# Revit family: PEFY-WP25VMS1-E_Service_Area1
name_source: partatom
category: Mechanical Equipment
revit_build: Autodesk Revit Architecture 2012 (Build: 20110916_2132(x64)
units: mm (PartAtom-declared; Revit-internal decimal feet)

## types (6) — shared parameters
Airflow Rate_High (m3/h) = 540
Airflow Rate_High (m3/min) = 9
Airflow Rate_Low (m3/h) = 330
Airflow Rate_Low (m3/min) = 5.5
Airflow Rate_Mid (m3/h) = 420
Airflow Rate_Mid (m3/min) = 7
Cooling Capacity (kW) = 2.8
Cooling Current (A) = 0.51
Cooling Power Input (kW) = 0.06
Depth = 700 mm  [stored 2.29659 ft]
Description = Ceiling concealed
Drain pipe1_radius = 16 mm  [stored 0.0524934 ft]
Drain pipe2_radius = 16 mm  [stored 0.0524934 ft]
External Finish = Galvanized steel plate
External_static_pressure (Pa) = 5-15-35-50
Fan Motor Output (kW) = 0.096
Fan_Quantity = 2
Fan_Type = Sirocco fan
Heating Capacity (kW) = 3.2
Heating Current (A) = 0.4
Heating Power Input (kW) = 0.04
Height = 200 mm  [stored 0.656168 ft]
Manufacturer = Mitsubishi Electric Corporation
Maximum Circuit Ampacity (A) = 0.75
Model = PEFY-WP25VMS1-E
Phase = 1
Protection Device = Fuse
Sound Pressure Level_High (dB(A)) = 30
Sound Pressure Level_Low (dB(A)) = 23
Sound Pressure Level_Mid (dB(A)) = 26
Space View = Yes
Subcategory = HVAC
URL = http://www.mitsubishielectric.com
Unit Weight (kg) = 20
Water Pipe_radius (From HBC Unit) = 13 mm
Water Pipe_radius (To HBC Unit) = 13 mm
Width = 790 mm  [stored 2.59186 ft]
zero-valued in all types: Equip_No., SerialNumber, TagNumber

## per-type parameters (varying)
| type | Hertz | Voltage |
| PEFY-WP25VMS1-E_220V_50Hz | 50 Hz | 220 V |
| PEFY-WP25VMS1-E_220V_60Hz | 60 Hz | 220 V |
| PEFY-WP25VMS1-E_230V_50Hz | 50 Hz | 230 V |
| PEFY-WP25VMS1-E_230V_60Hz | 60 Hz | 230 V |
| PEFY-WP25VMS1-E_240V_50Hz | 50 Hz | 240 V |
| PEFY-WP25VMS1-E_240V_60Hz | 60 Hz | 240 V |

note: [stored X ft] marks values corroborated as IEEE doubles in the binary element streams (Revit-internal decimal feet)

## geometry (parser evidence)
native form markers: Blend x16, Sweep x3
no freeform markers — native parametric forms only
